# Revit family: Electronics_Expansion-Inputs_Biamp_Vocia_Paging-Station-Interface_VPSI-1__
name_source: partatom
category: Communication Devices
units: mm (PartAtom-declared; Revit-internal decimal feet)

## family parameters
Cut with Voids When Loaded = No
Host = Face
Maintain Annotation Orientation = No
OmniClass Number = 23.85.10.11.11
OmniClass Title = Sound and Signal Devices
Part Type = Normal
Room Calculation Point = No
Round Connector Dimension = Use Diameter
Shared = No

## types (1)
- VPSI-1
    Altitude = 0-10,000 ft (0-3000m) MSL
    Apparent Load = 0 VA
    Compliance = CE marked (Europe) RoHS Directive (Europe)
    Connector Description = RJ-45; Power by the host device
    Default Elevation = 4' - 0"
    Depth = 0' - 6 1/8"
    Description = Vocia® VPSI-1 Paging Station Interface
    Effective Input Headroom = 25dB
    Frequency Response = 20Hz ~ 10kHz: +0, -1dB
    Height = 0' - 1 3/16"
    Housing Material = Biamp - Metal - Silver
    Humidity = 0-95% relative humidity (non-condensing)
    LED Output Voltage = 15mA
    Manufacturer = Biamp
    Max Power Consumption = 0 W
    Model = Vocia VPSI-1
    Network Connection = RJ45 with shielded Ethernet (CAT5, CAT5e, CAT6, or CAT7)
    Nominal Input Level = 0dBu, -10dBu, -40dBu and -50dBu (hardware configurable)
    Number of Poles = 1
    Power Factor = 1
    Product Documentation Link = https://downloads.biamp.com
    Product Page URL = https://www.biamp.com
    Product data url = https://www.bimobject.com
    RS-232 Baud = 57600 bps
    RS-232 Data Bits = 8
    RS-232 Flow Control = None
    RS-232 Parity = None
    RS-232 Stop Bits = 1
    THD+N = 20Hz ~ 10kHz: <0.08%
    Temperature Range = 23 - 104° F (-5 – 40° C)
    URL = https://www.biamp.com
    Voltage = 0 V
    Weight = 0.66 lbf
    Width = 0' - 3 5/32"

## geometry (parser evidence)
native form markers: Sweep x2
no freeform markers — native parametric forms only
